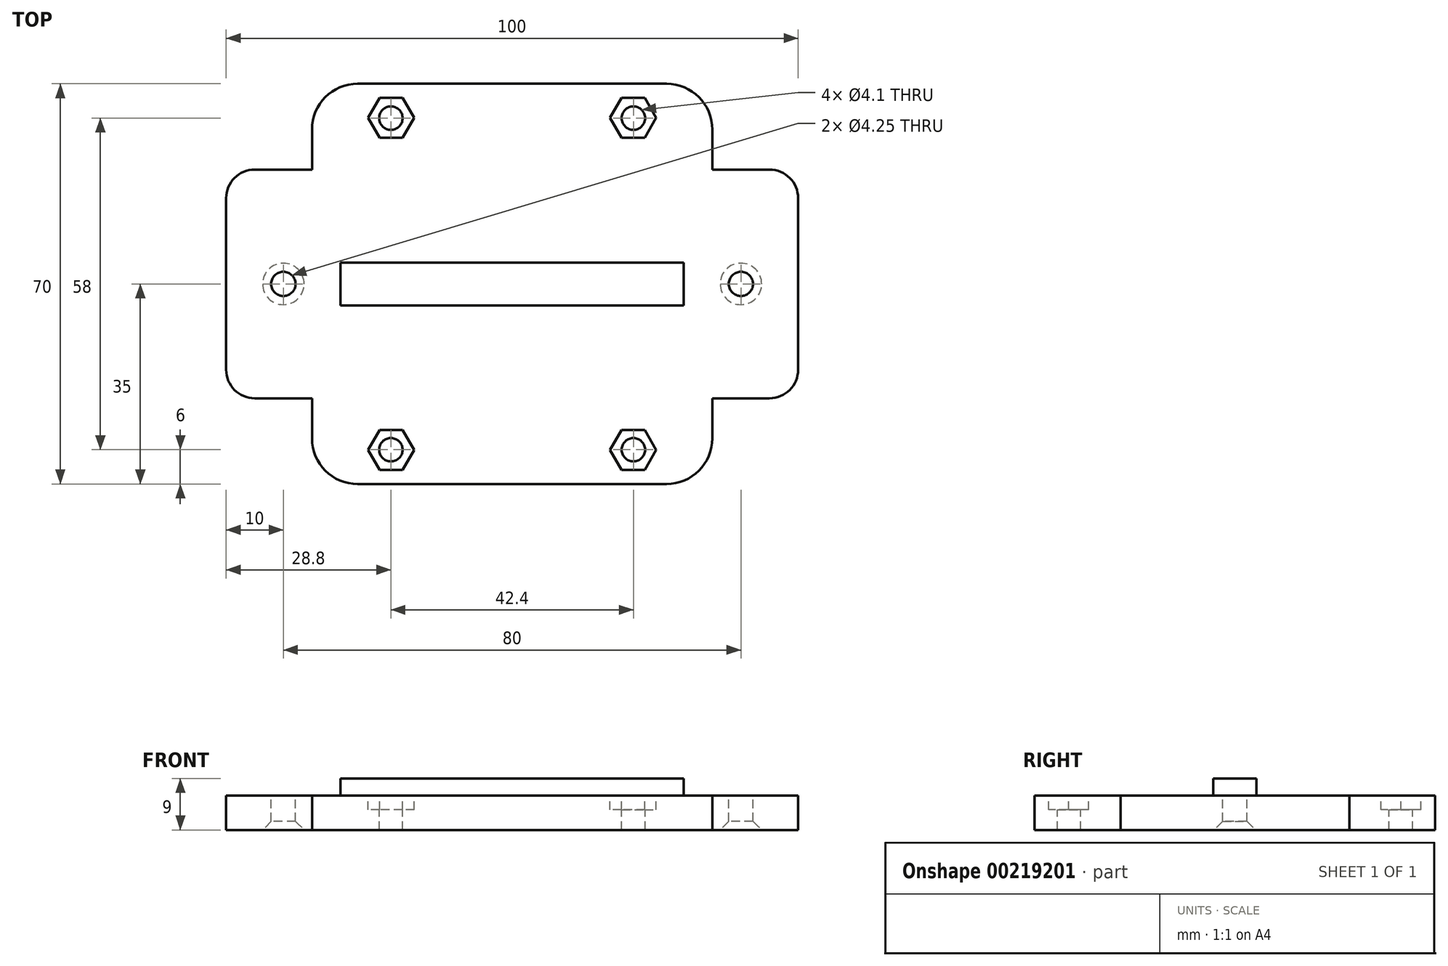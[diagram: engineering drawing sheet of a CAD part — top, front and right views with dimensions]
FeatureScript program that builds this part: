
annotation { "Feature Type Name" : "Feature", "Feature Type Description" : "" }
export const myFeature = defineFeature(function(context is Context, id is Id, definition is map)
    precondition{}
    {
        {
            var Q0;
            Q0=qCreatedBy(makeId("Top.planeOp"),FACE);
            var sketch = newSketch(context, id + "F0", { "sketchPlane" : qUnion([Q0])});
            skLineSegment(sketch, "E0.bottom", {"start": v(27, 35) * mm, "end": v(-27, 35) * mm});
            skLineSegment(sketch, "E0.top", {"start": v(27, -35) * mm, "end": v(-27, -35) * mm});
            skLineSegment(sketch, "E0.left", {"start": v(35, 27) * mm, "end": v(35, -27) * mm});
            skLineSegment(sketch, "E0.right", {"start": v(-35, 27) * mm, "end": v(-35, -27) * mm});
            skPoint(sketch, "E0.middle", {"position": v(0, 0) * mm});
            skPoint(sketch, "E1.visualSharp", {"position": v(-35, 35) * mm});
            skArc(sketch, "E1.filletArc", {"start": v(-27, 35) * mm, "mid": v(-32.66, 32.66) * mm, "end": v(-35, 27) * mm});
            skPoint(sketch, "E2.visualSharp", {"position": v(35, 35) * mm});
            skArc(sketch, "E2.filletArc", {"start": v(35, 27) * mm, "mid": v(32.66, 32.66) * mm, "end": v(27, 35) * mm});
            skPoint(sketch, "E3.visualSharp", {"position": v(35, -35) * mm});
            skArc(sketch, "E3.filletArc", {"start": v(27, -35) * mm, "mid": v(32.66, -32.66) * mm, "end": v(35, -27) * mm});
            skPoint(sketch, "E4.visualSharp", {"position": v(-35, -35) * mm});
            skArc(sketch, "E4.filletArc", {"start": v(-35, -27) * mm, "mid": v(-32.66, -32.66) * mm, "end": v(-27, -35) * mm});
            skLineSegment(sketch, "E5.bottom", {"start": v(45, 20) * mm, "end": v(-45, 20) * mm});
            skLineSegment(sketch, "E5.top", {"start": v(45, -20) * mm, "end": v(-45, -20) * mm});
            skLineSegment(sketch, "E5.left", {"start": v(50, 15) * mm, "end": v(50, -15) * mm});
            skLineSegment(sketch, "E5.right", {"start": v(-50, 15) * mm, "end": v(-50, -15) * mm});
            skPoint(sketch, "E6.visualSharp", {"position": v(-50, 20) * mm});
            skArc(sketch, "E6.filletArc", {"start": v(-45, 20) * mm, "mid": v(-48.54, 18.54) * mm, "end": v(-50, 15) * mm});
            skPoint(sketch, "E7.visualSharp", {"position": v(-50, -20) * mm});
            skArc(sketch, "E7.filletArc", {"start": v(-50, -15) * mm, "mid": v(-48.54, -18.54) * mm, "end": v(-45, -20) * mm});
            skPoint(sketch, "E8.visualSharp", {"position": v(50, -20) * mm});
            skArc(sketch, "E8.filletArc", {"start": v(45, -20) * mm, "mid": v(48.54, -18.54) * mm, "end": v(50, -15) * mm});
            skPoint(sketch, "E9.visualSharp", {"position": v(50, 20) * mm});
            skArc(sketch, "E9.filletArc", {"start": v(50, 15) * mm, "mid": v(48.54, 18.54) * mm, "end": v(45, 20) * mm});
            skLineSegment(sketch, "E10.bottom", {"start": v(30, 3.75) * mm, "end": v(-30, 3.75) * mm});
            skLineSegment(sketch, "E10.top", {"start": v(30, -3.75) * mm, "end": v(-30, -3.75) * mm});
            skLineSegment(sketch, "E10.left", {"start": v(30, 3.75) * mm, "end": v(30, -3.75) * mm});
            skLineSegment(sketch, "E10.right", {"start": v(-30, 3.75) * mm, "end": v(-30, -3.75) * mm});
            skCircle(sketch, "E11", {"center": v(-40, 0) * mm, "radius": 2.12 * mm});
            skCircle(sketch, "E12.MirrorC", {"center": v(40, 0) * mm, "radius": 2.12 * mm});
            skLineSegment(sketch, "E13.bottom", {"start": v(21.2, 29) * mm, "end": v(-21.2, 29) * mm, "construction": true});
            skLineSegment(sketch, "E13.top", {"start": v(21.2, -29) * mm, "end": v(-21.2, -29) * mm, "construction": true});
            skLineSegment(sketch, "E13.left", {"start": v(21.2, 29) * mm, "end": v(21.2, -29) * mm, "construction": true});
            skLineSegment(sketch, "E13.right", {"start": v(-21.2, 29) * mm, "end": v(-21.2, -29) * mm, "construction": true});
            skCircle(sketch, "E14", {"center": v(-21.2, 29) * mm, "radius": 2.05 * mm});
            skCircle(sketch, "E15.MirrorC", {"center": v(21.2, 29) * mm, "radius": 2.05 * mm});
            skCircle(sketch, "E16.MirrorC", {"center": v(21.2, -29) * mm, "radius": 2.05 * mm});
            skCircle(sketch, "E17.MirrorC", {"center": v(-21.2, -29) * mm, "radius": 2.05 * mm});
            skSolve(sketch);
        }
        {
            var Q0;
            Q0=makeQuery(id+"F0.imprint","IMPRINT",FACE,{"disambiguationData":[TD([[makeQuery(id+"F0.imprint","IMPRINT",EDGE,{"derivedFrom":sQuery(id+"F0.wireOp",EDGE,"E17.MirrorC")}),-1.0]])]});
            var Q1;
            Q1=makeQuery(id+"F0.imprint","IMPRINT",FACE,{"disambiguationData":[TD([[makeQuery(id+"F0.imprint","IMPRINT",EDGE,{"derivedFrom":sQuery(id+"F0.wireOp",EDGE,"E5.left")}),-1.0]])]});
            var Q2;
            Q2=makeQuery(id+"F0.imprint","IMPRINT",FACE,{"disambiguationData":[TD([[makeQuery(id+"F0.imprint","IMPRINT",EDGE,{"derivedFrom":sQuery(id+"F0.wireOp",EDGE,"E10.bottom")}),1.0]])]});
            var Q3;
            Q3=makeQuery(id+"F0.imprint","IMPRINT",FACE,{"disambiguationData":[TD([[makeQuery(id+"F0.imprint","IMPRINT",EDGE,{"derivedFrom":sQuery(id+"F0.wireOp",EDGE,"E5.right")}),1.0]])]});
            var Q4;
            Q4=makeQuery(id+"F0.imprint","IMPRINT",FACE,{"disambiguationData":[TD([[makeQuery(id+"F0.imprint","IMPRINT",EDGE,{"derivedFrom":sQuery(id+"F0.wireOp",EDGE,"E0.bottom")}),1.0]])]});
            var Q5;
            Q5=makeQuery(id+"F0.imprint","IMPRINT",FACE,{"disambiguationData":[TD([[makeQuery(id+"F0.imprint","IMPRINT",EDGE,{"derivedFrom":sQuery(id+"F0.wireOp",EDGE,"E0.top")}),-1.0]])]});
            var Q6;
            Q6=makeQuery(id+"F0.imprint","IMPRINT",FACE,{"disambiguationData":[TD([[makeQuery(id+"F0.imprint","IMPRINT",EDGE,{"derivedFrom":sQuery(id+"F0.wireOp",EDGE,"E10.bottom")}),-1.0]])]});
            extrude(context, id + "F1", {"entities" : qUnion([Q0, Q1, Q2, Q3, Q4, Q5, Q6]), "oppositeDirection" : true, "depth" : 6 * mm});
        }
        {
            var Q0;
            Q0=makeQuery(id+"F0.imprint","IMPRINT",FACE,{"disambiguationData":[TD([[makeQuery(id+"F0.imprint","IMPRINT",EDGE,{"derivedFrom":sQuery(id+"F0.wireOp",EDGE,"E10.bottom")}),1.0]])]});
            extrude(context, id + "F2", {"entities" : qUnion([Q0]), "operationType" : NewBodyOperationType.ADD, "depth" : 3 * mm});
        }
        {
            var Q0;
            Q0=makeQuery(id+"F1.opExtrude","CAP_EDGE",EDGE,{"disambiguationData":[OSD([sQuery(id+"F0.wireOp",EDGE,"E11")])],"isStart":false});
            var Q1;
            Q1=makeQuery(id+"F1.opExtrude","CAP_EDGE",EDGE,{"disambiguationData":[OSD([sQuery(id+"F0.wireOp",EDGE,"E12.MirrorC")])],"isStart":false});
            chamfer(context, id + "F3", {"entities" : qUnion([Q0, Q1]), "width" : 1.5 * mm, "tangentPropagation" : true});
        }
        {
            var Q0;
            Q0=qCreatedBy(makeId("Top.planeOp"),FACE);
            var sketch = newSketch(context, id + "F4", { "sketchPlane" : qUnion([Q0])});
            skCircle(sketch, "E18.cCircle", {"center": v(21.15, -29.06) * mm, "radius": 3.5 * mm, "construction": true});
            skLineSegment(sketch, "E18.0", {"start": v(23.17, -32.56) * mm, "end": v(19.13, -32.56) * mm});
            skLineSegment(sketch, "E18.1", {"start": v(19.13, -32.56) * mm, "end": v(17.1, -29.06) * mm});
            skLineSegment(sketch, "E18.2", {"start": v(17.1, -29.06) * mm, "end": v(19.13, -25.56) * mm});
            skLineSegment(sketch, "E18.3", {"start": v(19.13, -25.56) * mm, "end": v(23.17, -25.56) * mm});
            skLineSegment(sketch, "E18.4", {"start": v(23.17, -25.56) * mm, "end": v(25.2, -29.06) * mm});
            skLineSegment(sketch, "E18.5", {"start": v(25.2, -29.06) * mm, "end": v(23.17, -32.56) * mm});
            skPoint(sketch, "E18.0.midPoint", {"position": v(21.15, -32.56) * mm});
            skLineSegment(sketch, "E19.MirrorCS", {"start": v(-19.13, -25.56) * mm, "end": v(-23.17, -25.56) * mm});
            skLineSegment(sketch, "E20.MirrorCS", {"start": v(-17.1, -29.06) * mm, "end": v(-19.13, -25.56) * mm});
            skLineSegment(sketch, "E21.MirrorCS", {"start": v(-19.13, -32.56) * mm, "end": v(-17.1, -29.06) * mm});
            skLineSegment(sketch, "E22.MirrorCS", {"start": v(-23.17, -32.56) * mm, "end": v(-19.13, -32.56) * mm});
            skLineSegment(sketch, "E23.MirrorCS", {"start": v(-25.2, -29.06) * mm, "end": v(-23.17, -32.56) * mm});
            skLineSegment(sketch, "E24.MirrorCS", {"start": v(-23.17, -25.56) * mm, "end": v(-25.2, -29.06) * mm});
            skLineSegment(sketch, "E25.MirrorCS", {"start": v(-19.13, 25.56) * mm, "end": v(-23.17, 25.56) * mm});
            skLineSegment(sketch, "E26.MirrorCS", {"start": v(-23.17, 25.56) * mm, "end": v(-25.2, 29.06) * mm});
            skLineSegment(sketch, "E27.MirrorCS", {"start": v(-25.2, 29.06) * mm, "end": v(-23.17, 32.56) * mm});
            skLineSegment(sketch, "E28.MirrorCS", {"start": v(-23.17, 32.56) * mm, "end": v(-19.13, 32.56) * mm});
            skLineSegment(sketch, "E29.MirrorCS", {"start": v(-19.13, 32.56) * mm, "end": v(-17.1, 29.06) * mm});
            skLineSegment(sketch, "E30.MirrorCS", {"start": v(-17.1, 29.06) * mm, "end": v(-19.13, 25.56) * mm});
            skLineSegment(sketch, "E31.MirrorCS", {"start": v(17.1, 29.06) * mm, "end": v(19.13, 25.56) * mm});
            skLineSegment(sketch, "E32.MirrorCS", {"start": v(19.13, 32.56) * mm, "end": v(17.1, 29.06) * mm});
            skLineSegment(sketch, "E33.MirrorCS", {"start": v(23.17, 32.56) * mm, "end": v(19.13, 32.56) * mm});
            skLineSegment(sketch, "E34.MirrorCS", {"start": v(25.2, 29.06) * mm, "end": v(23.17, 32.56) * mm});
            skLineSegment(sketch, "E35.MirrorCS", {"start": v(23.17, 25.56) * mm, "end": v(25.2, 29.06) * mm});
            skLineSegment(sketch, "E36.MirrorCS", {"start": v(19.13, 25.56) * mm, "end": v(23.17, 25.56) * mm});
            skCircle(sketch, "E37.MirrorC", {"center": v(21.15, 29.06) * mm, "radius": 3.5 * mm, "construction": true});
            skSolve(sketch);
        }
        {
            var Q0;
            Q0=makeQuery(id+"F4.imprint","IMPRINT",FACE,{"disambiguationData":[TD([[makeQuery(id+"F4.imprint","IMPRINT",EDGE,{"derivedFrom":sQuery(id+"F4.wireOp",EDGE,"E18.0")}),-1.0]])]});
            var Q1;
            Q1=makeQuery(id+"F4.imprint","IMPRINT",FACE,{"disambiguationData":[TD([[makeQuery(id+"F4.imprint","IMPRINT",EDGE,{"derivedFrom":sQuery(id+"F4.wireOp",EDGE,"E19.MirrorCS")}),1.0]])]});
            var Q2;
            Q2=makeQuery(id+"F4.imprint","IMPRINT",FACE,{"disambiguationData":[TD([[makeQuery(id+"F4.imprint","IMPRINT",EDGE,{"derivedFrom":sQuery(id+"F4.wireOp",EDGE,"E25.MirrorCS")}),-1.0]])]});
            var Q3;
            Q3=makeQuery(id+"F4.imprint","IMPRINT",FACE,{"disambiguationData":[TD([[makeQuery(id+"F4.imprint","IMPRINT",EDGE,{"derivedFrom":sQuery(id+"F4.wireOp",EDGE,"E31.MirrorCS")}),1.0]])]});
            extrude(context, id + "F5", {"entities" : qUnion([Q0, Q1, Q2, Q3]), "operationType" : NewBodyOperationType.REMOVE, "oppositeDirection" : true, "depth" : 2.5 * mm});
        }
    });
